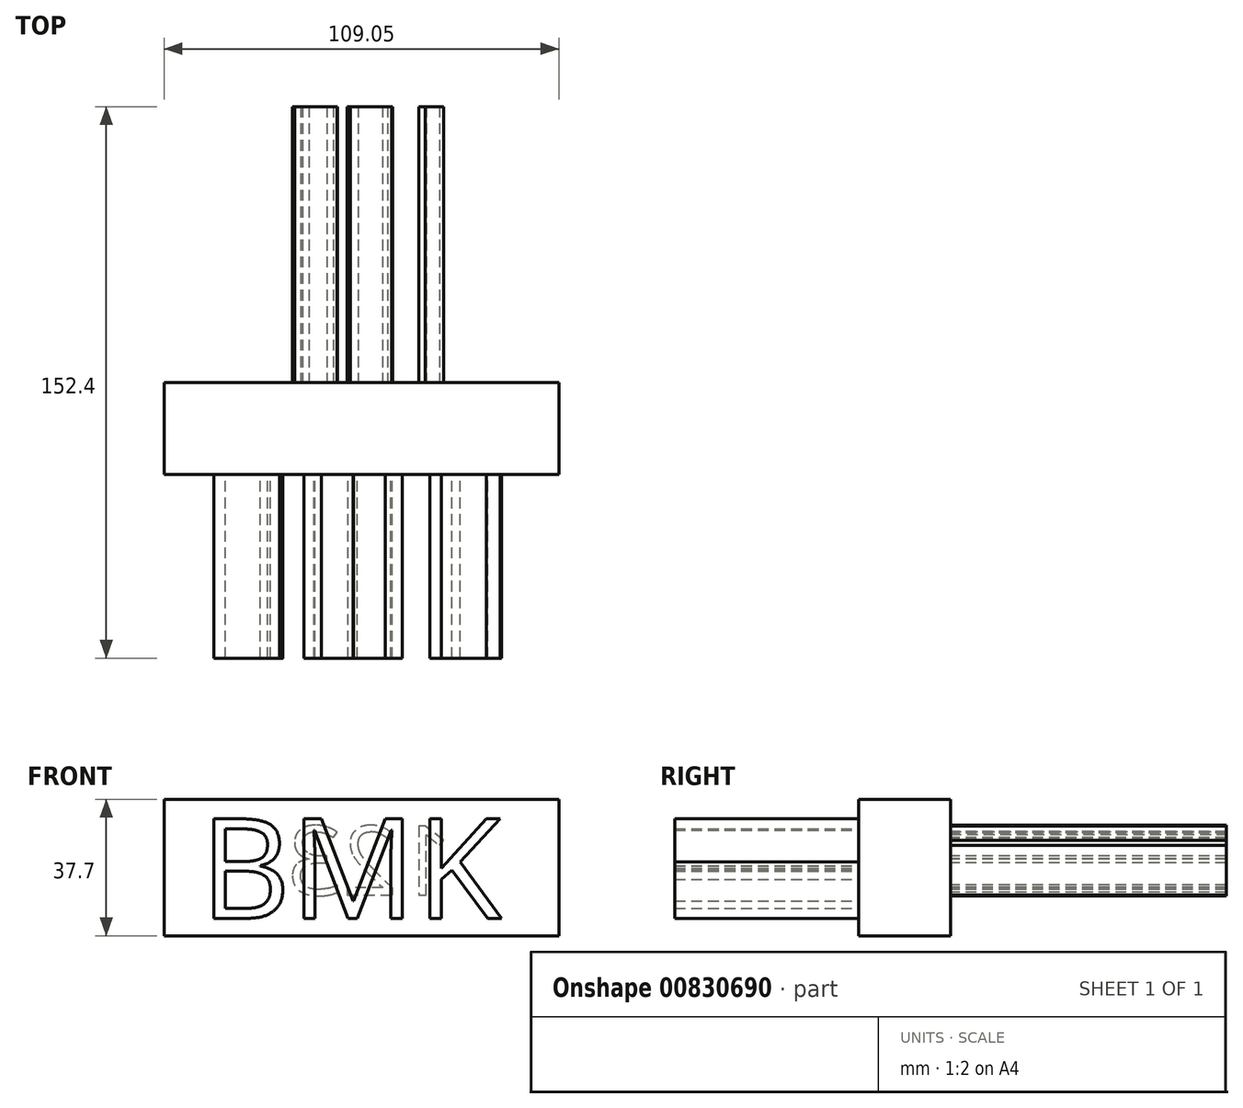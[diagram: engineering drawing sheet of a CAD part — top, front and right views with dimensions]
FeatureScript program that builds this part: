
annotation { "Feature Type Name" : "Feature", "Feature Type Description" : "" }
export const myFeature = defineFeature(function(context is Context, id is Id, definition is map)
    precondition{}
    {
        {
            var Q0;
            Q0=qCreatedBy(makeId("Front.planeOp"),FACE);
            var sketch = newSketch(context, id + "F0", { "sketchPlane" : qUnion([Q0])});
            skLineSegment(sketch, "E0.bottom", {"start": v(0, 0) * mm, "end": v(109.05, 0) * mm});
            skLineSegment(sketch, "E0.top", {"start": v(0, 37.7) * mm, "end": v(109.05, 37.7) * mm});
            skLineSegment(sketch, "E0.left", {"start": v(0, 0) * mm, "end": v(0, 37.7) * mm});
            skLineSegment(sketch, "E0.right", {"start": v(109.05, 0) * mm, "end": v(109.05, 37.7) * mm});
            skSolve(sketch);
        }
        {
            var Q0;
            Q0=makeQuery(id+"F0.imprint","IMPRINT",FACE,{"disambiguationData":[TD([[makeQuery(id+"F0.imprint","IMPRINT",EDGE,{"derivedFrom":sQuery(id+"F0.wireOp",EDGE,"E0.bottom")}),1.0]])]});
            extrude(context, id + "F1", {"entities" : qUnion([Q0]), "depth" : 25.4 * mm, "offsetDistance" : 25.4 * mm});
        }
        {
            var Q0;
            Q0=makeQuery(id+"F1.opExtrude","CAP_FACE",FACE,{"disambiguationData":[OSD([sQuery(id+"F0.wireOp",EDGE,"E0.bottom"),sQuery(id+"F0.wireOp",EDGE,"E0.top"),sQuery(id+"F0.wireOp",EDGE,"E0.left"),sQuery(id+"F0.wireOp",EDGE,"E0.right")])],"isStart":false});
            var sketch = newSketch(context, id + "F2", { "sketchPlane" : qUnion([Q0])});
            skSolve(sketch);
        }
        {
            var Q0;
            Q0=makeQuery(id+"F2.imprint","IMPRINT",FACE,{"disambiguationData":[TD([[makeQuery(id+"F2.imprint","IMPRINT",EDGE,{"derivedFrom":makeQuery(id+"F1.opExtrude","CAP_EDGE",EDGE,{"disambiguationData":[OSD([sQuery(id+"F0.wireOp",EDGE,"E0.bottom")])],"isStart":false})}),1.0]])]});
            var sketch = newSketch(context, id + "F3", { "sketchPlane" : qUnion([Q0])});
            skText(sketch, "E1", { "text": "BMK", "fontName": "OpenSans-Regular.ttf"});
            const initialGuessF3  = {"E1": [0.00998, 0.00483, 1, 0, 0.02769]};
            skSetInitialGuess(sketch, initialGuessF3);
            skSolve(sketch);
        }
        {
            var Q0;
            Q0 = qSketchRegion(id + "F3", true);
            extrude(context, id + "F4", {"entities" : qUnion([Q0]), "operationType" : NewBodyOperationType.ADD, "depth" : 50.8 * mm, "offsetDistance" : 25.4 * mm});
        }
        {
            var Q0;
            Q0=makeQuery(id+"F1.opExtrude","CAP_FACE",FACE,{"disambiguationData":[OSD([sQuery(id+"F0.wireOp",EDGE,"E0.bottom"),sQuery(id+"F0.wireOp",EDGE,"E0.top"),sQuery(id+"F0.wireOp",EDGE,"E0.left"),sQuery(id+"F0.wireOp",EDGE,"E0.right")])],"isStart":true});
            var sketch = newSketch(context, id + "F5", { "sketchPlane" : qUnion([Q0])});
            skText(sketch, "E2", { "text": "123", "fontName": "OpenSans-Regular.ttf"});
            const initialGuessF5  = {"E2": [-0.07966, 0.01125, 1, 0, 0.01921]};
            skSetInitialGuess(sketch, initialGuessF5);
            skSolve(sketch);
        }
        {
            var Q0;
            Q0 = qSketchRegion(id + "F5", true);
            extrude(context, id + "F6", {"entities" : qUnion([Q0]), "operationType" : NewBodyOperationType.ADD, "depth" : 76.2 * mm, "offsetDistance" : 25.4 * mm});
        }
    });
